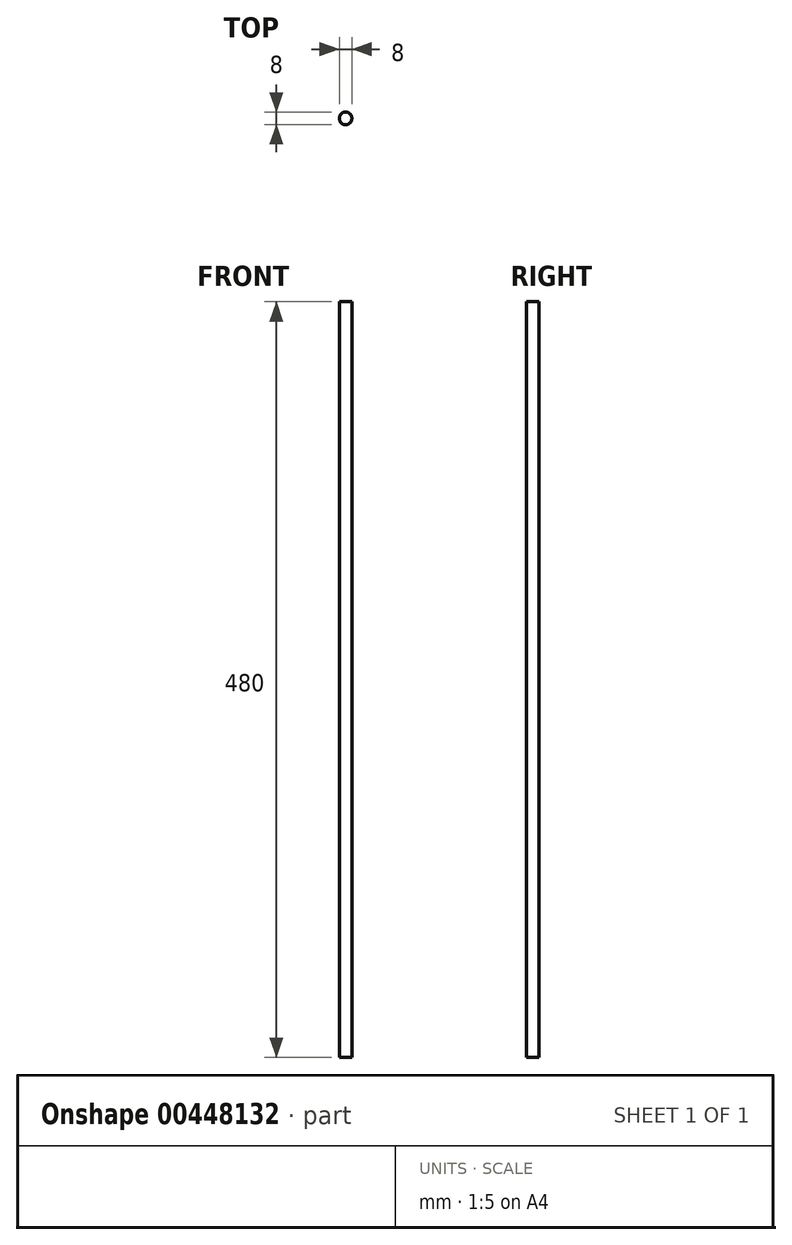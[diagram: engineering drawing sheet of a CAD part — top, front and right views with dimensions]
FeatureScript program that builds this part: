
annotation { "Feature Type Name" : "Feature", "Feature Type Description" : "" }
export const myFeature = defineFeature(function(context is Context, id is Id, definition is map)
    precondition{}
    {
        {
            var Q0;
            Q0=qCreatedBy(makeId("Top.planeOp"),FACE);
            var sketch = newSketch(context, id + "F0", { "sketchPlane" : qUnion([Q0])});
            skCircle(sketch, "E0", {"center": v(0, 0) * mm, "radius": 4 * mm});
            skSolve(sketch);
        }
        {
            var Q0;
            Q0 = qSketchRegion(id + "F0", true);
            extrude(context, id + "F1", {"entities" : qUnion([Q0]), "depth" : 480 * mm});
        }
    });
